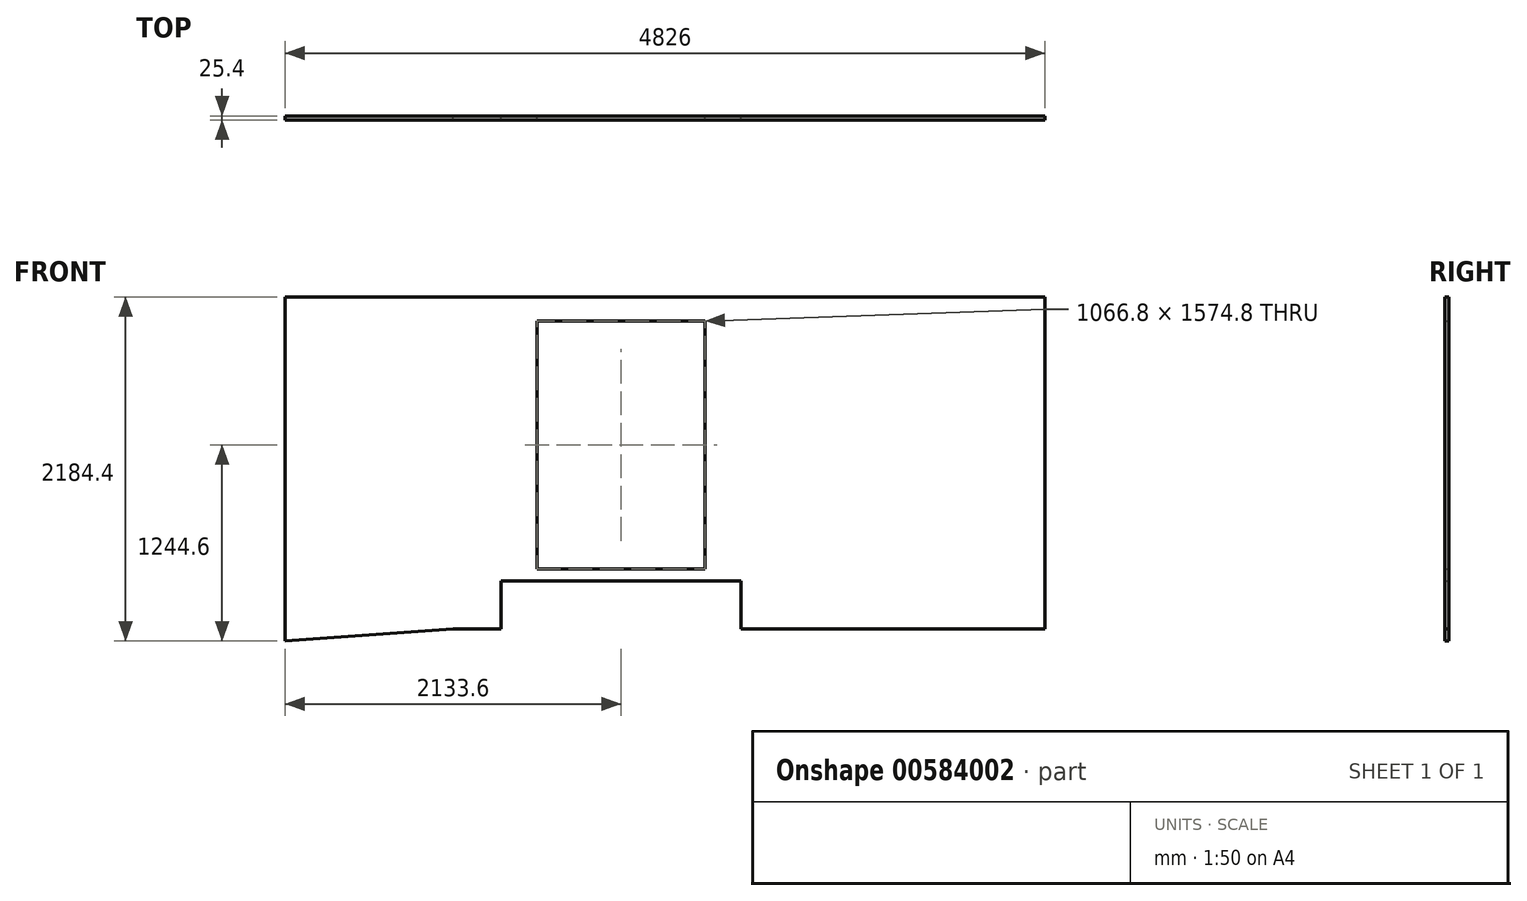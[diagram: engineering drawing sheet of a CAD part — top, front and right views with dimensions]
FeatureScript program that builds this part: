
annotation { "Feature Type Name" : "Feature", "Feature Type Description" : "" }
export const myFeature = defineFeature(function(context is Context, id is Id, definition is map)
    precondition{}
    {
        {
            var Q0;
            Q0=qCreatedBy(makeId("Front.planeOp"),FACE);
            var sketch = newSketch(context, id + "F0", { "sketchPlane" : qUnion([Q0])});
            skLineSegment(sketch, "E0", {"start": v(-1367.11, -857.03) * mm, "end": v(-1062.31, -857.03) * mm});
            skLineSegment(sketch, "E1", {"start": v(-1062.31, -552.23) * mm, "end": v(461.69, -552.23) * mm});
            skLineSegment(sketch, "E2", {"start": v(461.69, -552.23) * mm, "end": v(461.69, -857.03) * mm});
            skLineSegment(sketch, "E3", {"start": v(461.69, -857.03) * mm, "end": v(2392.09, -857.03) * mm});
            skLineSegment(sketch, "E4", {"start": v(2392.09, -857.03) * mm, "end": v(2392.09, 1251.17) * mm});
            skLineSegment(sketch, "E5", {"start": v(2392.09, 1251.17) * mm, "end": v(-2433.91, 1251.17) * mm});
            skLineSegment(sketch, "E6", {"start": v(-2433.91, 1251.17) * mm, "end": v(-2433.91, -933.23) * mm});
            skLineSegment(sketch, "E7", {"start": v(-1062.31, -552.23) * mm, "end": v(-1062.31, -857.03) * mm});
            skLineSegment(sketch, "E8", {"start": v(-1367.11, 1251.17) * mm, "end": v(-1367.11, -857.03) * mm, "construction": true});
            skPoint(sketch, "E9.orphan", {"position": v(-1367.11, 0) * mm});
            skLineSegment(sketch, "E10", {"start": v(-1367.11, -857.03) * mm, "end": v(-2433.91, -933.23) * mm});
            skLineSegment(sketch, "E11", {"start": v(-833.71, -476.03) * mm, "end": v(-833.71, 1098.77) * mm});
            skLineSegment(sketch, "E12", {"start": v(-833.71, 1098.77) * mm, "end": v(233.09, 1098.77) * mm});
            skLineSegment(sketch, "E13", {"start": v(233.09, 1098.77) * mm, "end": v(233.09, -476.03) * mm});
            skLineSegment(sketch, "E14", {"start": v(233.09, -476.03) * mm, "end": v(-833.71, -476.03) * mm});
            skLineSegment(sketch, "E15", {"start": v(461.69, -831.63) * mm, "end": v(2392.09, -831.63) * mm, "construction": true});
            skLineSegment(sketch, "E16", {"start": v(-1062.31, -831.63) * mm, "end": v(-1367.11, -831.63) * mm, "construction": true});
            skLineSegment(sketch, "E17", {"start": v(-1367.11, -831.63) * mm, "end": v(-2433.91, -907.83) * mm, "construction": true});
            skSolve(sketch);
        }
        {
            var Q0;
            Q0=makeQuery(id+"F0.imprint","IMPRINT",FACE,{"disambiguationData":[TD([[makeQuery(id+"F0.imprint","IMPRINT",EDGE,{"derivedFrom":sQuery(id+"F0.wireOp",EDGE,"E0")}),1.0]])]});
            extrude(context, id + "F1", {"entities" : qUnion([Q0]), "depth" : 25.4 * mm, "offsetDistance" : 25.4 * mm});
        }
    });
